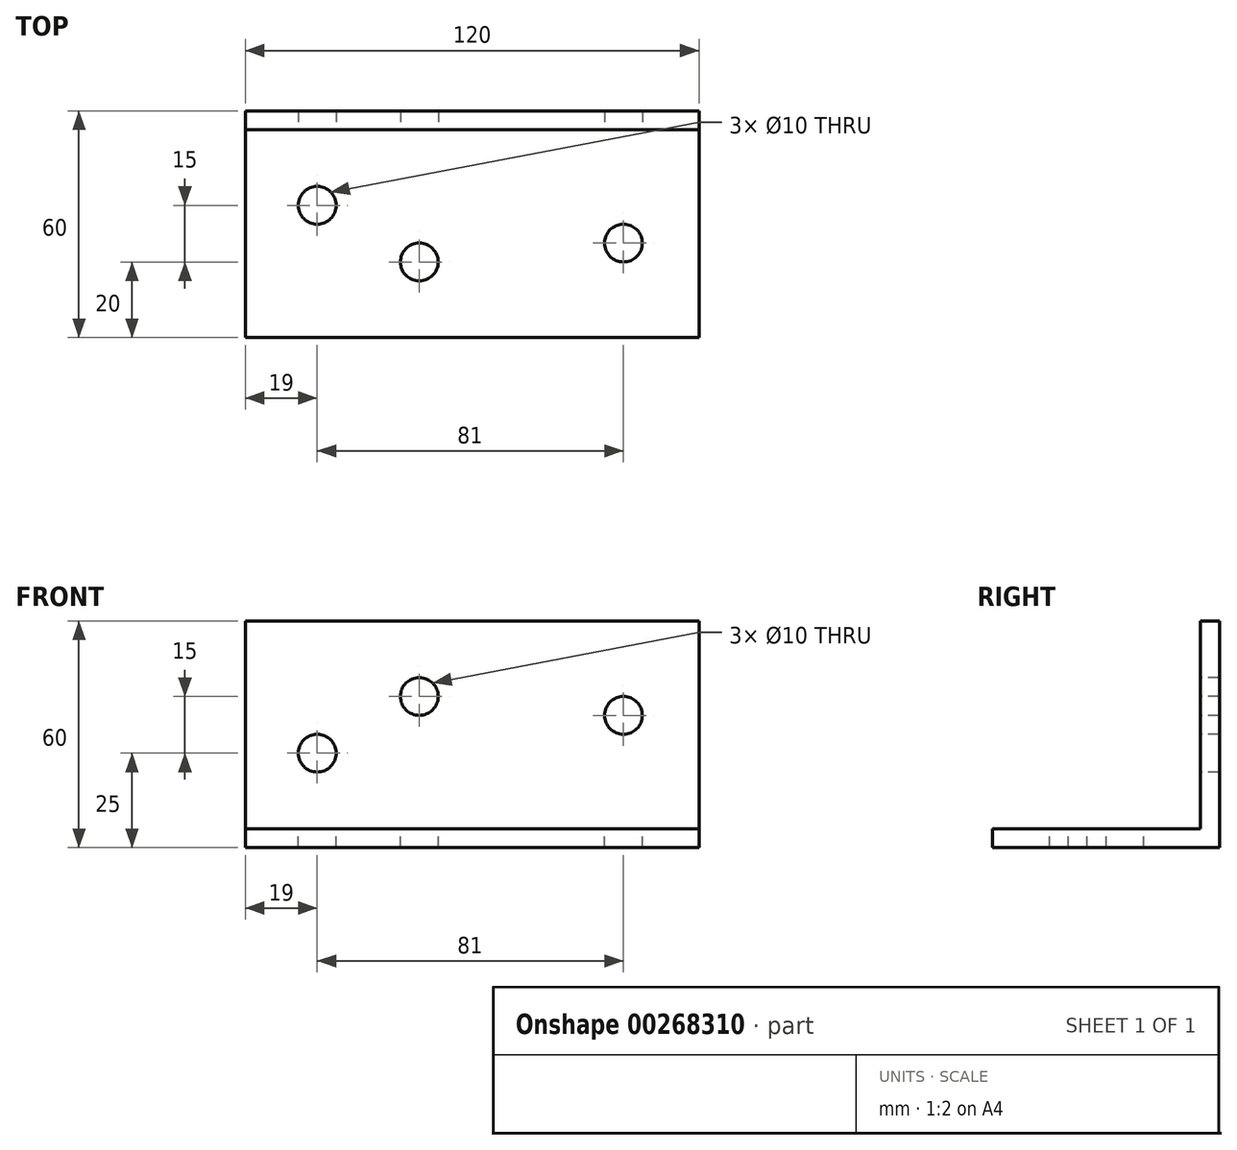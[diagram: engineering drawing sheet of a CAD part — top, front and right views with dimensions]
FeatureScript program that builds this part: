
annotation { "Feature Type Name" : "Feature", "Feature Type Description" : "" }
export const myFeature = defineFeature(function(context is Context, id is Id, definition is map)
    precondition{}
    {
        {
            var Q0;
            Q0=qCreatedBy(makeId("Right.planeOp"),FACE);
            var sketch = newSketch(context, id + "F0", { "sketchPlane" : qUnion([Q0])});
            skLineSegment(sketch, "E0", {"start": v(0, 0) * mm, "end": v(60, 0) * mm});
            skLineSegment(sketch, "E1", {"start": v(60, 0) * mm, "end": v(60, 60) * mm});
            skLineSegment(sketch, "E2", {"start": v(60, 60) * mm, "end": v(55, 60) * mm});
            skLineSegment(sketch, "E3", {"start": v(55, 60) * mm, "end": v(55, 5) * mm});
            skLineSegment(sketch, "E4", {"start": v(55, 5) * mm, "end": v(0, 5) * mm});
            skLineSegment(sketch, "E5", {"start": v(0, 5) * mm, "end": v(0, 0) * mm});
            skSolve(sketch);
        }
        {
            var Q0;
            Q0=qSketchRegion(id+"F0",true);
            extrude(context, id + "F1", {"entities" : qUnion([Q0]), "depth" : 120 * mm});
        }
        {
            var Q0;
            Q0=makeQuery(id+"F1.opExtrude","SWEPT_FACE",FACE,{"disambiguationData":[OSD([sQuery(id+"F0.wireOp",EDGE,"E4")])]});
            var sketch = newSketch(context, id + "F2", { "sketchPlane" : qUnion([Q0])});
            skCircle(sketch, "E6", {"center": v(19, 35) * mm, "radius": 5 * mm});
            skCircle(sketch, "E7", {"center": v(46, 20) * mm, "radius": 5 * mm});
            skSolve(sketch);
        }
        {
            var Q0;
            Q0=makeQuery(id+"F1.opExtrude","SWEPT_FACE",FACE,{"disambiguationData":[OSD([sQuery(id+"F0.wireOp",EDGE,"E3")])]});
            var sketch = newSketch(context, id + "F3", { "sketchPlane" : qUnion([Q0])});
            skCircle(sketch, "E8", {"center": v(19, 25) * mm, "radius": 5 * mm});
            skCircle(sketch, "E9", {"center": v(46, 40) * mm, "radius": 5 * mm});
            skSolve(sketch);
        }
        {
            var Q0;
            Q0=sQuery(id+"F2.wireOp",VERTEX,"E7.center");
            var Q1;
            Q1=sQuery(id+"F2.wireOp",VERTEX,"E6.center");
            var Q2;
            Q2=sQuery(id+"F3.wireOp",VERTEX,"E9.center");
            var Q3;
            Q3=sQuery(id+"F3.wireOp",VERTEX,"E8.center");
            var Q4;
            Q4=makeQuery(id+"F1.opExtrude","SWEPT_BODY",BODY,{"disambiguationData":[OSD([sQuery(id+"F0.wireOp",EDGE,"E0"),sQuery(id+"F0.wireOp",EDGE,"E1"),sQuery(id+"F0.wireOp",EDGE,"E2"),sQuery(id+"F0.wireOp",EDGE,"E3"),sQuery(id+"F0.wireOp",EDGE,"E4"),sQuery(id+"F0.wireOp",EDGE,"E5")])]});
            hole(context, id + "F4", {"style" : HoleStyle.SIMPLE, "endStyle" : HoleEndStyle.THROUGH, "holeDiameter" : 10 * mm, "majorDiameter" : 5 * mm, "tappedDepth" : 12 * mm, "tapClearance" : 3, "locations" : qUnion([Q0, Q1, Q2, Q3]), "scope" : qUnion([Q4])});
        }
        {
            var Q0;
            Q0=makeQuery(id+"F1.opExtrude","SWEPT_FACE",FACE,{"disambiguationData":[OSD([sQuery(id+"F0.wireOp",EDGE,"E3")])]});
            var sketch = newSketch(context, id + "F5", { "sketchPlane" : qUnion([Q0])});
            skCircle(sketch, "E10", {"center": v(100, 35) * mm, "radius": 2.05 * mm});
            skSolve(sketch);
        }
        {
            var Q0;
            Q0=sQuery(id+"F5.wireOp",VERTEX,"E10.center");
            var Q1;
            Q1=makeQuery(id+"F1.opExtrude","SWEPT_BODY",BODY,{"disambiguationData":[OSD([sQuery(id+"F0.wireOp",EDGE,"E0"),sQuery(id+"F0.wireOp",EDGE,"E1"),sQuery(id+"F0.wireOp",EDGE,"E2"),sQuery(id+"F0.wireOp",EDGE,"E3"),sQuery(id+"F0.wireOp",EDGE,"E4"),sQuery(id+"F0.wireOp",EDGE,"E5")])]});
            hole(context, id + "F6", {"style" : HoleStyle.SIMPLE, "endStyle" : HoleEndStyle.THROUGH, "holeDiameter" : 10 * mm, "majorDiameter" : 5 * mm, "tappedDepth" : 12 * mm, "tapClearance" : 3, "locations" : qUnion([Q0]), "scope" : qUnion([Q1])});
        }
        {
            var Q0;
            Q0=makeQuery(id+"F1.opExtrude","SWEPT_FACE",FACE,{"disambiguationData":[OSD([sQuery(id+"F0.wireOp",EDGE,"E4")])]});
            var sketch = newSketch(context, id + "F7", { "sketchPlane" : qUnion([Q0])});
            skCircle(sketch, "E11", {"center": v(100, 25) * mm, "radius": 7.1 * mm});
            skSolve(sketch);
        }
        {
            var Q0;
            Q0=sQuery(id+"F7.wireOp",VERTEX,"E11.center");
            var Q1;
            Q1=makeQuery(id+"F1.opExtrude","SWEPT_BODY",BODY,{"disambiguationData":[OSD([sQuery(id+"F0.wireOp",EDGE,"E0"),sQuery(id+"F0.wireOp",EDGE,"E1"),sQuery(id+"F0.wireOp",EDGE,"E2"),sQuery(id+"F0.wireOp",EDGE,"E3"),sQuery(id+"F0.wireOp",EDGE,"E4"),sQuery(id+"F0.wireOp",EDGE,"E5")])]});
            hole(context, id + "F8", {"style" : HoleStyle.SIMPLE, "endStyle" : HoleEndStyle.THROUGH, "holeDiameter" : 10 * mm, "majorDiameter" : 5 * mm, "tappedDepth" : 12 * mm, "tapClearance" : 3, "locations" : qUnion([Q0]), "scope" : qUnion([Q1])});
        }
    });
